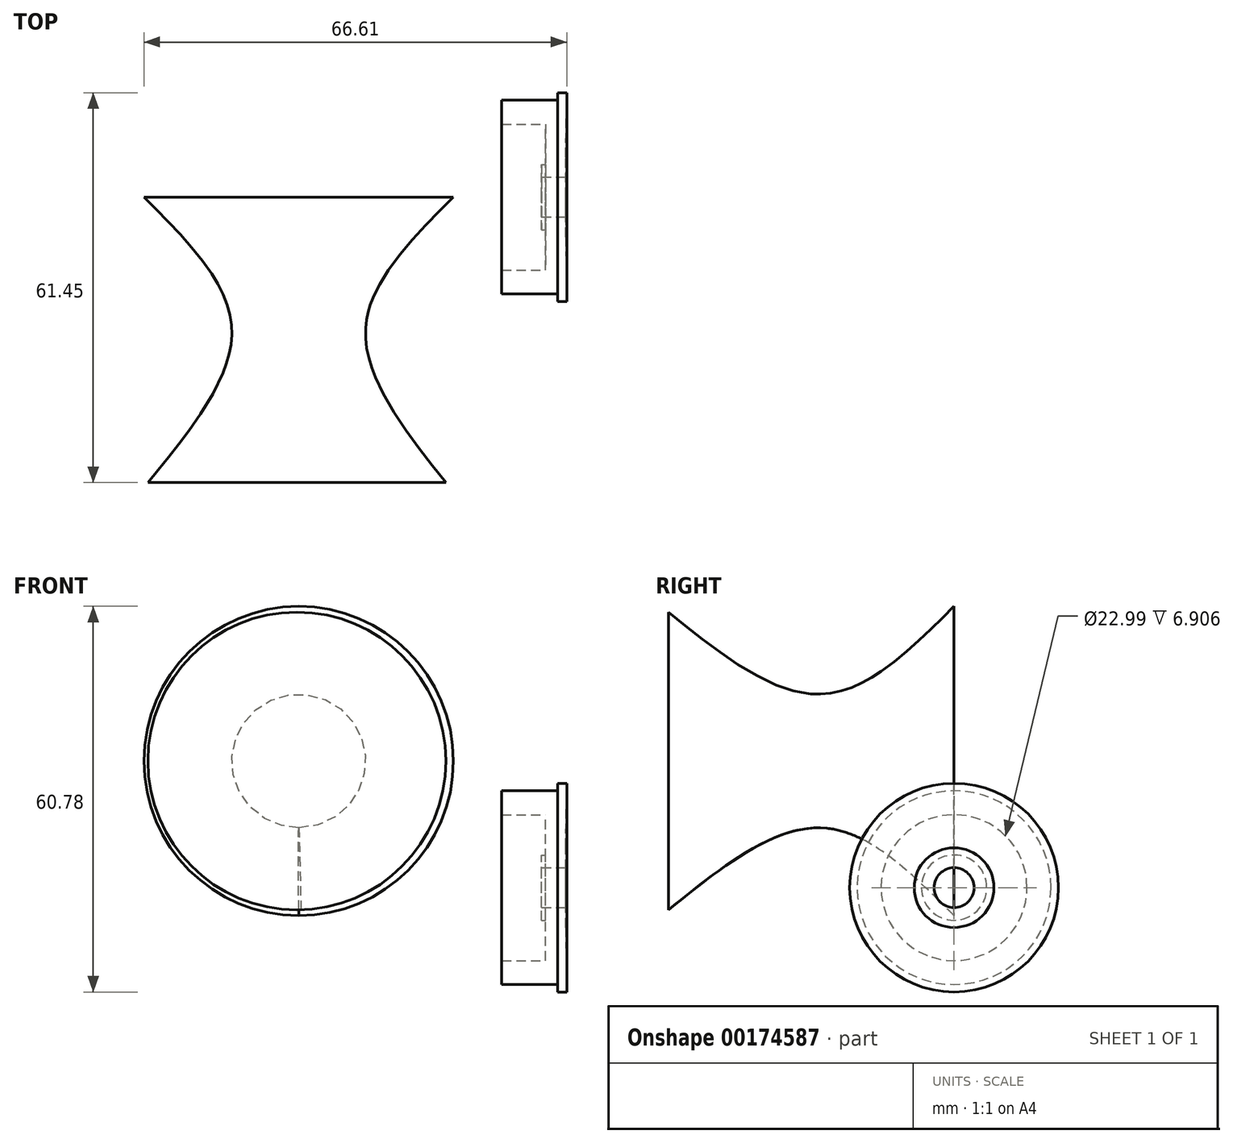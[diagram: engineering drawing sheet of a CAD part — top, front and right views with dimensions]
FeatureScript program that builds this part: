
annotation { "Feature Type Name" : "Feature", "Feature Type Description" : "" }
export const myFeature = defineFeature(function(context is Context, id is Id, definition is map)
    precondition{}
    {
        {
            var Q0;
            Q0=qCreatedBy(makeId("Front.planeOp"),FACE);
            var sketch = newSketch(context, id + "F0", { "sketchPlane" : qUnion([Q0])});
            skLineSegment(sketch, "E0", {"start": v(-1.46, 7.66) * mm, "end": v(-3.98, 7.66) * mm});
            skLineSegment(sketch, "E1", {"start": v(-3.98, 7.66) * mm, "end": v(-3.98, 9.66) * mm});
            skLineSegment(sketch, "E2", {"start": v(-3.98, 9.66) * mm, "end": v(-3.35, 9.66) * mm});
            skLineSegment(sketch, "E3", {"start": v(-3.35, 9.66) * mm, "end": v(-3.35, 16.02) * mm});
            skLineSegment(sketch, "E4", {"start": v(-3.35, 16.02) * mm, "end": v(-10.25, 16.02) * mm});
            skLineSegment(sketch, "E5", {"start": v(-10.25, 16.02) * mm, "end": v(-10.25, 19.78) * mm});
            skLineSegment(sketch, "E6", {"start": v(-10.25, 19.78) * mm, "end": v(-3.35, 19.78) * mm});
            skLineSegment(sketch, "E7", {"start": v(-3.35, 19.78) * mm, "end": v(-1.46, 19.78) * mm});
            skLineSegment(sketch, "E8", {"start": v(-1.46, 7.66) * mm, "end": v(-0.2, 7.66) * mm});
            skLineSegment(sketch, "E9", {"start": v(-0.2, 7.66) * mm, "end": v(-0.2, 10.8) * mm});
            skLineSegment(sketch, "E10", {"start": v(12.99, 4.52) * mm, "end": v(-20.86, 4.52) * mm});
            skLineSegment(sketch, "E11", {"start": v(-1.46, 19.78) * mm, "end": v(-1.46, 20.97) * mm});
            skLineSegment(sketch, "E12", {"start": v(-1.46, 20.97) * mm, "end": v(0, 20.97) * mm});
            skLineSegment(sketch, "E13", {"start": v(0, 20.97) * mm, "end": v(-0.2, 10.8) * mm});
            skSolve(sketch);
        }
        {
            var Q0;
            Q0 = qSketchRegion(id + "F0", true);
            var Q1;
            Q1=sQuery(id+"F0.wireOp",EDGE,"E10");
            revolve(context, id + "F1", {"entities" : qUnion([Q0]), "axis" : qUnion([Q1]), "revolveType" : RevolveType.FULL});
        }
        {
            var Q0;
            Q0=qCreatedBy(makeId("Front.planeOp"),FACE);
            var sketch = newSketch(context, id + "F2", { "sketchPlane" : qUnion([Q0])});
            skCircle(sketch, "E14", {"center": v(-42.23, 24.5) * mm, "radius": 24.37 * mm});
            skSolve(sketch);
        }
        {
            var Q0;
            Q0=qCreatedBy(makeId("Front.planeOp"),FACE);
            cPlane(context, id + "F3", {"entities" : qUnion([Q0]), "cplaneType" : CPlaneType.OFFSET, "offset" : 20 * mm, "width" : 150 * mm, "height" : 150 * mm});
        }
        {
            var Q0;
            Q0=qCreatedBy(id+"F3.planeOp",FACE);
            var sketch = newSketch(context, id + "F4", { "sketchPlane" : qUnion([Q0])});
            skCircle(sketch, "E15", {"center": v(-42.23, 24.5) * mm, "radius": 10.6 * mm});
            skSolve(sketch);
        }
        {
            var Q0;
            Q0=qCreatedBy(id+"F3.planeOp",FACE);
            cPlane(context, id + "F5", {"entities" : qUnion([Q0]), "cplaneType" : CPlaneType.OFFSET, "offset" : 25 * mm, "width" : 150 * mm, "height" : 150 * mm});
        }
        {
            var Q0;
            Q0=qCreatedBy(id+"F5.planeOp",FACE);
            var sketch = newSketch(context, id + "F6", { "sketchPlane" : qUnion([Q0])});
            skCircle(sketch, "E16", {"center": v(-42.53, 24.5) * mm, "radius": 23.47 * mm});
            skSolve(sketch);
        }
        {
            var Q0;
            Q0=makeQuery(id+"F2.imprint","IMPRINT",FACE,{"disambiguationData":[TD([[makeQuery(id+"F2.imprint","IMPRINT",EDGE,{"derivedFrom":sQuery(id+"F2.wireOp",EDGE,"E14")}),1.0]])]});
            var Q1;
            Q1=makeQuery(id+"F4.imprint","IMPRINT",FACE,{"disambiguationData":[TD([[makeQuery(id+"F4.imprint","IMPRINT",EDGE,{"derivedFrom":sQuery(id+"F4.wireOp",EDGE,"E15")}),1.0]])]});
            var Q2;
            Q2=makeQuery(id+"F6.imprint","IMPRINT",FACE,{"disambiguationData":[TD([[makeQuery(id+"F6.imprint","IMPRINT",EDGE,{"derivedFrom":sQuery(id+"F6.wireOp",EDGE,"E16")}),1.0]])]});
            loft(context, id + "F7", {"sheetProfilesArray" : [{ "sheetProfileEntities" : qUnion([Q0]) }, { "sheetProfileEntities" : qUnion([Q1]) }, { "sheetProfileEntities" : qUnion([Q2]) }]});
        }
    });
